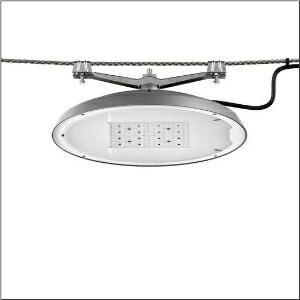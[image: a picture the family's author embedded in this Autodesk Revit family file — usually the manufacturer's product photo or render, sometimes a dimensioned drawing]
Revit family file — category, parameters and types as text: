
# Revit family: dl_r__50_iq_mini___st1_0s_5xa248w31f08le_ba39
name_source: partatom
category: Lighting Fixtures
units: mm (PartAtom-declared; Revit-internal decimal feet)

## family parameters
Cut with Voids When Loaded = No
Host = Face
Light Source = No
Part Type = Normal
Room Calculation Point = No
Round Connector Dimension = Use Diameter
Shared = No

## types (1)
- --- (1 x LED, 10390 lm, 67.4 W, 3000K)
    Apparent Load = 67 VA
    CIE Flux Codes = 37 72 97 100 100
    Color Rendering = 70
    Color Temperature = 3000K
    Default Elevation = 1800 mm
    Description = DL® 50 iQ mini, catenary luminaire, primary light control with lens, of PMMA, primary optical cover: cover, of toughened safety glass, transparent, light distribution: ST1.0s, light emission: direct distribution, primary light characteristic: symmetric, installation type: suspended mounting, LED, High Power LED, rated luminous flux: 10.390lm, luminous efficacy: 154lm/W, light colour: 730, colour temperature: 3000K, control gear: iQ Street-Remote, control: optimised constant luminous flux control (CLO 2.0), Desk-Remote (wireless, voltage-free reading and setting of iQ features in the workshop via application-optimized NFC function/RFID function), Light-Fading, Smart-Wire, Night-Set, Lumen-Switch, Temp-Guard, Auto-Match, Street-Remote, mains connection: 230..240V, AC, 50/60Hz, start of lifetime: 67W, end of service life: 70W, reduction: 31W, luminaire housing, of diecast aluminium, powder-coated, Siteco® metallic grey (DB 702S), diameter: 500mm, height: 115mm, mounting height: 4..12m, protection rating (complete): IP66, insulation class (complete): insulation class II (safety insulation), certification: CE, ENEC, ENEC+, VDE, impact resistance: IK08, permissible operating ambient temperature for outdoor applications: -25..+40°C, standard-compliant lighting for roads and squares, packaging unit: 1 piece

Light Distribution: ST1.0s
    Height = 124 mm  [stored 0.406824 ft]
    Lamp = 1 x LED
    Lamp Light Flux = 10390 lm
    Lamp Power = 67.4 W
    Lamp count = 1
    Length = 500 mm
    Luminous efficacy = 154 lm/W
    Manufacturer = Siteco
    ModVariant = No
    Model = 5XA248W31F08LE
    Number of Poles = 1
    OnlyDefault = Yes
    Power Factor = 1
    Product Name = DL® 50 iQ mini | ST1.0s
    Product group = catenary luminaire
    ProductGroupID = 6300
    Protection Class = Protection class II
    Protection Degree = IP 66
    RLX_Detail_Level = 1
    RLX_Emergency_Light_Flux = 0 lm
    RLX_Emergency_Type = 0
    RLX_Emergency_Type_DB = No
    RlxData = <blob elided: 126965 chars, md5=4655e456>
    Socket = socket
    Standby Power = 0 W
    System Light Flux = 10390 lm
    System Power = 67 W
    Type Comments = factory setting: luminous flux: 100 % | dim-lin: 254 | 705 mA
    Type Image = l_1251783.jpg
    URL = http://relux.com
    VarID = @adj_162005
    Voltage = 0 V
    Weight = 0.00 kg
    Width = 0 mm  [stored 0 ft]

note: [stored X ft] marks values corroborated as IEEE doubles in the binary element streams (Revit-internal decimal feet)

## geometry (parser evidence)
native form markers: Blend x4, Sweep x13
no freeform markers — native parametric forms only
